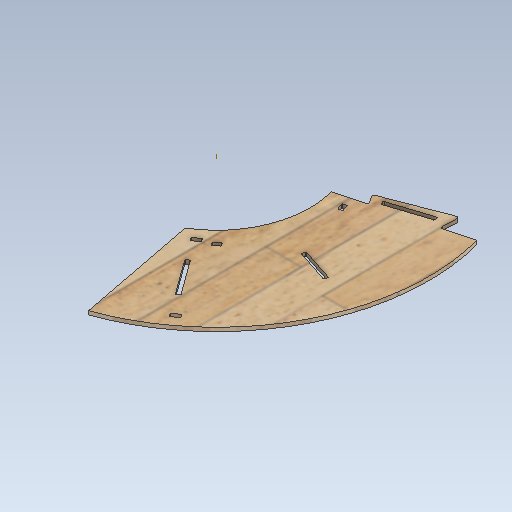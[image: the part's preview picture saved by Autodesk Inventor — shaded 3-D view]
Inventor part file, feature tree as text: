
AUTODESK INVENTOR PART (.ipt)
format: ipt  version: 2020 (Build 240168000, 168)  size: 585,216 bytes
history: native  units: mm
features: extrude x7, sketch x5, mirror x3, pattern_circular x3, plane x1
ambient origin geometry x8: Origin, YZ Plane, XZ Plane, XY Plane, X Axis, Y Axis, Z Axis, Center Point
bodies: Body1 (feature_tree)
feature tree (19):
  extrude  "Extrusion3"  Depth=6.5mm
  extrude  "Extrusion4"  Depth=2.666667mm
  extrude  "Extrusion5"  Depth=1.333333mm
  sketch  "Sketch5"  dims[d25=2.666667mm d32=1.333333mm]
  extrude  "Extrusion7"  TaperAngle=0.0deg  [1 undecoded]
  sketch  "Sketch7"  dims[d40=3.25mm d41=90.0deg d42=3.25mm d43=90.0deg d47=50.0mm d49=360.0deg d52=4.363323mm d54=10.0mm d55=0.0mm d60=0.872665mm d61=12.566371mm d62=13.439035mm d63=2.666667mm d64=0.523599mm d66=0.523599mm d67=2.666667mm d68=2.666667mm d70=12.566371mm d71=12.566371mm d84=300.14mm d85=682.72mm d86=491.43mm d87=150.07mm d88=341.36mm d89=4.363323mm d90=1.919862mm d91=1.919862mm d94=300.14mm d95=682.72mm d96=0.24305mm d104=6.5mm d105=12.0mm d108=1.333333mm d109=1.333333mm d110=1.333333mm d111=1.333333mm d112=0.0mm d113=0.0mm d114=0.0mm d116=1.333333mm d117=1.333333mm d119=1.333333mm d120=1.333333mm d121=6.5mm d122=10.0mm d123=0.0mm d124=0.0mm d126=1.09mm d127=16.333333mm d128=1.333333mm d129=1.333333mm d130=1.333333mm d131=1.333333mm d132=6.5mm d133=10.0mm d135=0.523599mm d137=0.0mm d138=0.0mm d140=0.666667mm d141=3.25mm d142=20.0mm d143=12.566371mm d145=20.0mm d146=12.566371mm d148=0.27mm d149=145.0mm d150=90.0deg d151=90.0deg d152=90.0deg d153=90.0deg d154=20.0mm d155=25.132741mm d157=0.0mm d158=0.0mm]
  extrude  "Extrusion8"  TaperAngle=90.0deg  [1 undecoded]
  extrude  "Extrusion9"  Depth=145.0mm
  plane  "Work Plane1"
  mirror  "Mirror2"
  mirror  "Mirror1"
  pattern_circular  "Circular Pattern1"  Angle=90.0deg  [1 undecoded]
  pattern_circular  "Circular Pattern2"  Count=5 Angle=360.0deg
  pattern_circular  "Circular Pattern3"  [2 undecoded]
  mirror  "Mirror3"
  extrude  "Extrusion10"  Depth=10.0mm TaperAngle=0.0deg
  sketch  "Sketch2"  dims[d15=6.0mm d16=0.0mm d21=6.5mm]
  sketch  "Sketch3"  dims[d23=66.666667mm d24=2.666667mm]
  sketch  "Sketch6"  dims[d33=1.333333mm d38=0.0mm d39=0.0mm]
note: 5 required parameter values undecoded (feature->parameter linkage not recoverable at this tier; creation-order binding heuristic only, values carry confidence <= 0.55)
